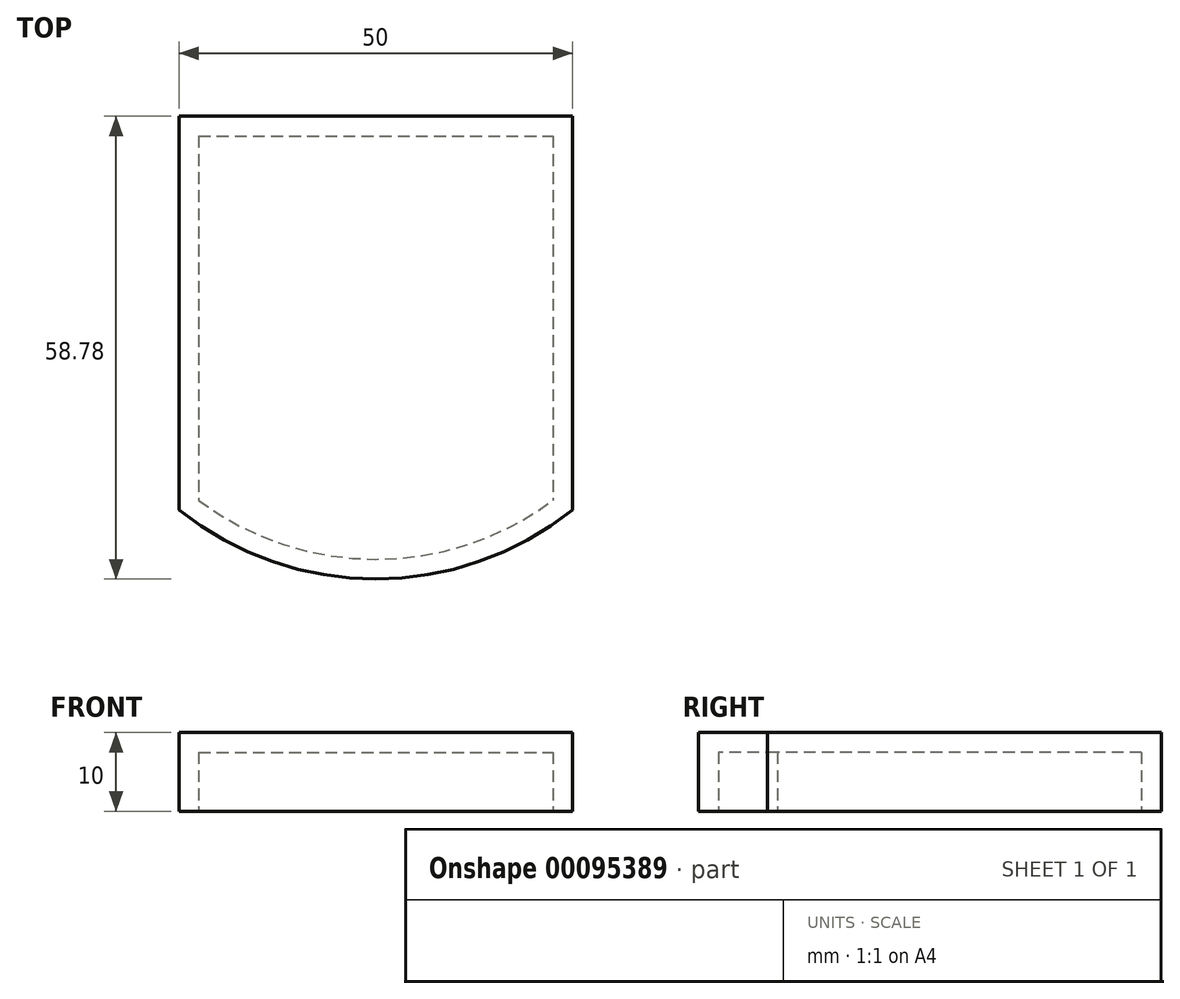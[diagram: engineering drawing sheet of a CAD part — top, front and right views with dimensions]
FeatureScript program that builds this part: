
annotation { "Feature Type Name" : "Feature", "Feature Type Description" : "" }
export const myFeature = defineFeature(function(context is Context, id is Id, definition is map)
    precondition{}
    {
        {
            var Q0;
            Q0=qCreatedBy(makeId("Top.planeOp"),FACE);
            var sketch = newSketch(context, id + "F0", { "sketchPlane" : qUnion([Q0])});
            skLineSegment(sketch, "E0.bottom", {"start": v(-25, 25) * mm, "end": v(25, 25) * mm});
            skLineSegment(sketch, "E0.top", {"start": v(-25, -25) * mm, "end": v(25, -25) * mm});
            skLineSegment(sketch, "E0.left", {"start": v(-25, 25) * mm, "end": v(-25, -25) * mm});
            skLineSegment(sketch, "E0.right", {"start": v(25, 25) * mm, "end": v(25, -25) * mm});
            skPoint(sketch, "E0.middle", {"position": v(0, 0) * mm});
            skArc(sketch, "E1", {"start": v(-25, -25) * mm, "mid": v(0, -33.78) * mm, "end": v(25, -25) * mm});
            skSolve(sketch);
        }
        {
            var Q0;
            Q0=makeQuery(id+"F0.imprint","IMPRINT",FACE,{"disambiguationData":[TD([[makeQuery(id+"F0.imprint","IMPRINT",EDGE,{"derivedFrom":sQuery(id+"F0.wireOp",EDGE,"E0.bottom")}),-1.0]])]});
            var Q1;
            Q1=makeQuery(id+"F0.imprint","IMPRINT",FACE,{"disambiguationData":[TD([[makeQuery(id+"F0.imprint","IMPRINT",EDGE,{"derivedFrom":sQuery(id+"F0.wireOp",EDGE,"E0.top")}),-1.0]])]});
            extrude(context, id + "F1", {"entities" : qUnion([Q0, Q1]), "depth" : 10 * mm});
        }
        {
            var Q0;
            Q0=makeQuery(id+"F1.opExtrude","CAP_FACE",FACE,{"disambiguationData":[OSD([sQuery(id+"F0.wireOp",EDGE,"E0.bottom"),sQuery(id+"F0.wireOp",EDGE,"E0.left"),sQuery(id+"F0.wireOp",EDGE,"E0.right"),sQuery(id+"F0.wireOp",EDGE,"E1")])],"isStart":true});
            shell(context, id + "F2", {"entities" : qUnion([Q0]), "thickness" : 2.5 * mm});
        }
    });
